# Revit family: Versailles 250
name_source: partatom
category: Lighting Fixtures
revit_build: Autodesk Revit 2018 (Build: 20170223_1515(x64)
units: mm (PartAtom-declared; Revit-internal decimal feet)

## family parameters
Always vertical = Yes
Cut with Voids When Loaded = No
Host = Wall
Light Source = Yes
OmniClass Number = 23.80.70.00
OmniClass Title = Lighting
Part Type = Normal
Room Calculation Point = No
Round Connector Dimension = Use Diameter
Shared = No

## types (3) — shared parameters
Color Filter = 16777215
Colour Temperature = 3000 K
Dimmable = No
Dimming Lamp Color Temperature Shift = <None>
Dimming Method = None
Driver Included = Yes
Driver Required = No
Efficacy (lm/w) = 78.72
Electrical Class = 2
Emit from Line Length = 610 mm
Lamp = LED
Light Source Fixed = Yes
Location rating = IP44
Luminous Flux = 370 lm
Main Material = Metal - Steel
Manufacturer = Astro Lighting Ltd
Model = Versailles 250
Photometric Web File = GNC-21391 Versailles 250 LED - 7961.ies
Power (Watts) = 4.7
Product Location = Bathroom/Indoor
Tilt Angle = 0.00°
URL = www.astrolighting.com

## per-type parameters (varying)
| type | Main Finish | Product Name | Product SKU |
| Astro Versaiiles Polished Chrome 1380001 | Polished Chrome | Versailles 250 Chrome | 1380001 |
| Astro Versailles 250 Bronze 1380004 | Bronze | Versailles 250 Bronze | 1380004 |
| Astro Versailles 250 Matt Gold 1380015 | Matt Gold | Versailles 250 Gold | 1380015 |

## geometry (parser evidence)
native form markers: Sweep x3
no freeform markers — native parametric forms only
